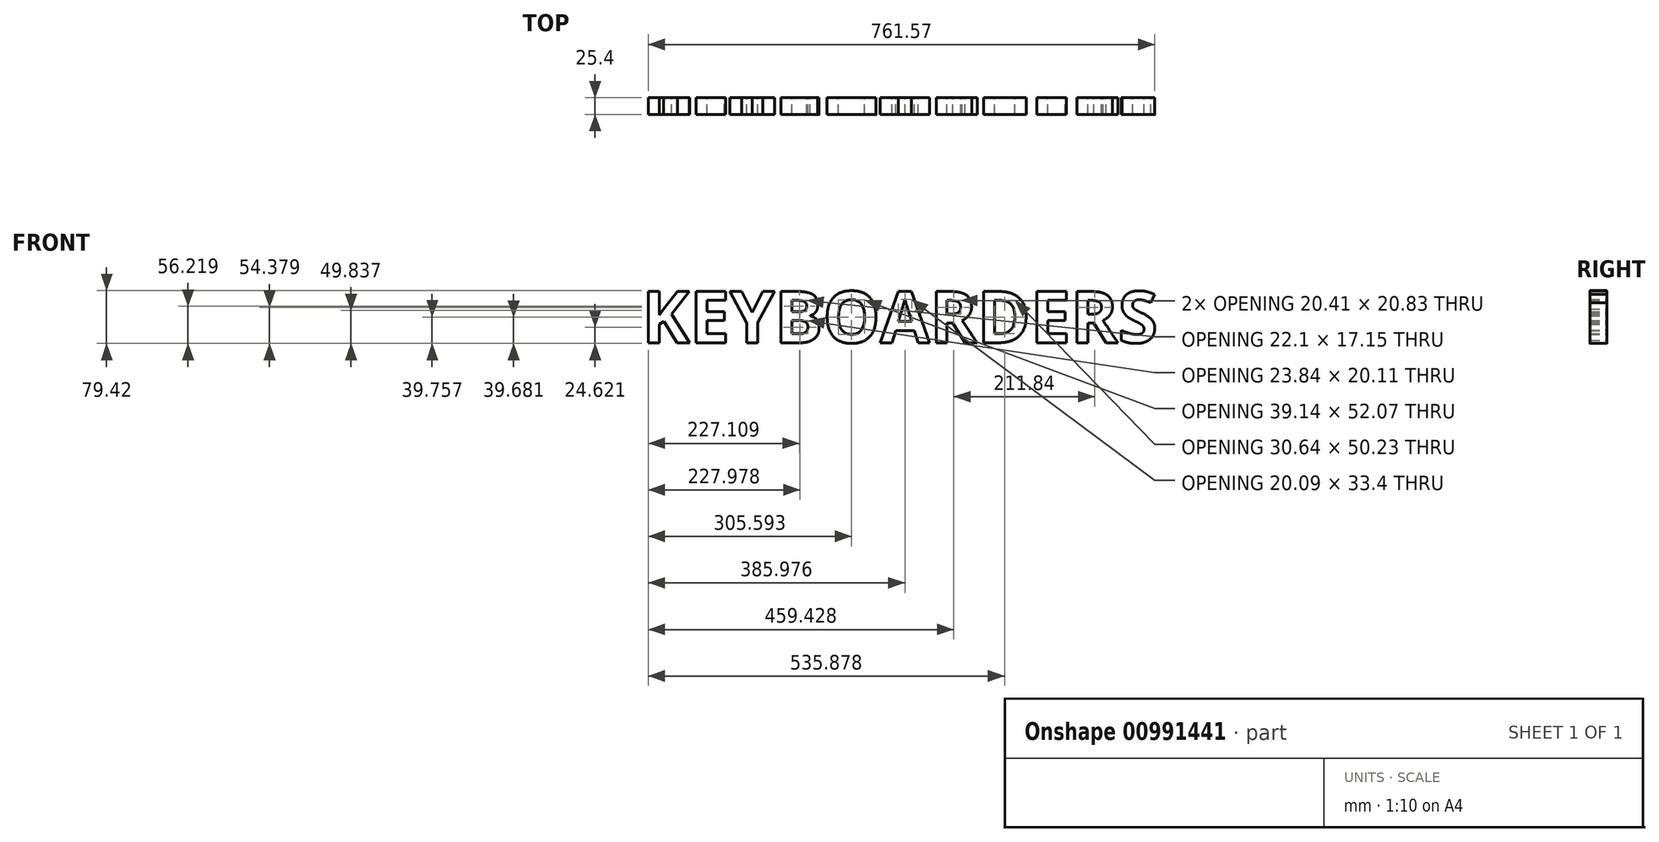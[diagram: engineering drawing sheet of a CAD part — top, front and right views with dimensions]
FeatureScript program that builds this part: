
annotation { "Feature Type Name" : "Feature", "Feature Type Description" : "" }
export const myFeature = defineFeature(function(context is Context, id is Id, definition is map)
    precondition{}
    {
        {
            var Q0;
            Q0=qCreatedBy(makeId("Front.planeOp"),FACE);
            var sketch = newSketch(context, id + "F0", { "sketchPlane" : qUnion([Q0])});
            skText(sketch, "E0", { "text": "KEYBOARDERS", "fontName": "OpenSans-Bold.ttf"});
            const initialGuessF0  = {"E0": [-0.37791, -0.03574, 1, 0, 0.0778]};
            skSetInitialGuess(sketch, initialGuessF0);
            skSolve(sketch);
        }
        {
            var Q0;
            Q0=makeQuery(id+"F0.imprint","IMPRINT",FACE,{"disambiguationData":[TD([[makeQuery(id+"F0.imprint","IMPRINT",EDGE,{"derivedFrom":sQuery(id+"F0.wireOp",EDGE,"E0.sketch_text.stroke-0")}),-1.0]])]});
            var Q1;
            Q1=makeQuery(id+"F0.imprint","IMPRINT",FACE,{"disambiguationData":[TD([[makeQuery(id+"F0.imprint","IMPRINT",EDGE,{"derivedFrom":sQuery(id+"F0.wireOp",EDGE,"E0.sketch_text.stroke-13")}),-1.0]])]});
            var Q2;
            Q2=makeQuery(id+"F0.imprint","IMPRINT",FACE,{"disambiguationData":[TD([[makeQuery(id+"F0.imprint","IMPRINT",EDGE,{"derivedFrom":sQuery(id+"F0.wireOp",EDGE,"E0.sketch_text.stroke-25")}),-1.0]])]});
            var Q3;
            Q3=makeQuery(id+"F0.imprint","IMPRINT",FACE,{"disambiguationData":[TD([[makeQuery(id+"F0.imprint","IMPRINT",EDGE,{"derivedFrom":sQuery(id+"F0.wireOp",EDGE,"E0.sketch_text.stroke-34")}),-1.0]])]});
            var Q4;
            Q4=makeQuery(id+"F0.imprint","IMPRINT",FACE,{"disambiguationData":[TD([[makeQuery(id+"F0.imprint","IMPRINT",EDGE,{"derivedFrom":sQuery(id+"F0.wireOp",EDGE,"E0.sketch_text.stroke-59")}),-1.0]])]});
            var Q5;
            Q5=makeQuery(id+"F0.imprint","IMPRINT",FACE,{"disambiguationData":[TD([[makeQuery(id+"F0.imprint","IMPRINT",EDGE,{"derivedFrom":sQuery(id+"F0.wireOp",EDGE,"E0.sketch_text.stroke-73")}),-1.0]])]});
            var Q6;
            Q6=makeQuery(id+"F0.imprint","IMPRINT",FACE,{"disambiguationData":[TD([[makeQuery(id+"F0.imprint","IMPRINT",EDGE,{"derivedFrom":sQuery(id+"F0.wireOp",EDGE,"E0.sketch_text.stroke-85")}),-1.0]])]});
            var Q7;
            Q7=makeQuery(id+"F0.imprint","IMPRINT",FACE,{"disambiguationData":[TD([[makeQuery(id+"F0.imprint","IMPRINT",EDGE,{"derivedFrom":sQuery(id+"F0.wireOp",EDGE,"E0.sketch_text.stroke-104")}),-1.0]])]});
            var Q8;
            Q8=makeQuery(id+"F0.imprint","IMPRINT",FACE,{"disambiguationData":[TD([[makeQuery(id+"F0.imprint","IMPRINT",EDGE,{"derivedFrom":sQuery(id+"F0.wireOp",EDGE,"E0.sketch_text.stroke-116")}),-1.0]])]});
            var Q9;
            Q9=makeQuery(id+"F0.imprint","IMPRINT",FACE,{"disambiguationData":[TD([[makeQuery(id+"F0.imprint","IMPRINT",EDGE,{"derivedFrom":sQuery(id+"F0.wireOp",EDGE,"E0.sketch_text.stroke-128")}),-1.0]])]});
            var Q10;
            Q10=makeQuery(id+"F0.imprint","IMPRINT",FACE,{"disambiguationData":[TD([[makeQuery(id+"F0.imprint","IMPRINT",EDGE,{"derivedFrom":sQuery(id+"F0.wireOp",EDGE,"E0.sketch_text.stroke-147")}),-1.0]])]});
            extrude(context, id + "F1", {"entities" : qUnion([Q0, Q1, Q2, Q3, Q4, Q5, Q6, Q7, Q8, Q9, Q10]), "depth" : 25.4 * mm, "offsetDistance" : 25.4 * mm});
        }
    });
